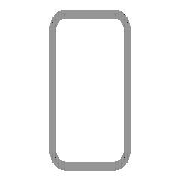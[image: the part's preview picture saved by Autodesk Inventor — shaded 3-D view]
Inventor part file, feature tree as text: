
AUTODESK INVENTOR PART (.ipt)
format: ipt  version: 2025.3 (Build 293356000, 356)  size: 133,632 bytes
history: native  units: mm (DEFAULTED — no unit token found)
features: other x4, sketch x1, plane x1
ambient origin geometry x8: Origin, YZ Plane, XZ Plane, XY Plane, X Axis, Y Axis, Z Axis, Center Point
bodies: Solid1 (feature_tree), Body (feature_tree)
feature tree (6):
  parser-record x1  (decoder bookkeeping rows leaked as tree rows — omitted from the tree; the rows remain in map.json)
  other  "Driven Length"
  other  "Start Plane"
  other  "End Plane"
  sketch  "Sketch3"  dims[d3=1000.0mm d4=0.0mm d7=6.0mm d9=40.0mm d11=80.0mm d12=3.0mm d13=80.0mm d14=1080.0mm d15=20.0mm d16=40.0mm d17=90.0deg d18=1000.0mm]
  plane  "Work Plane3"
